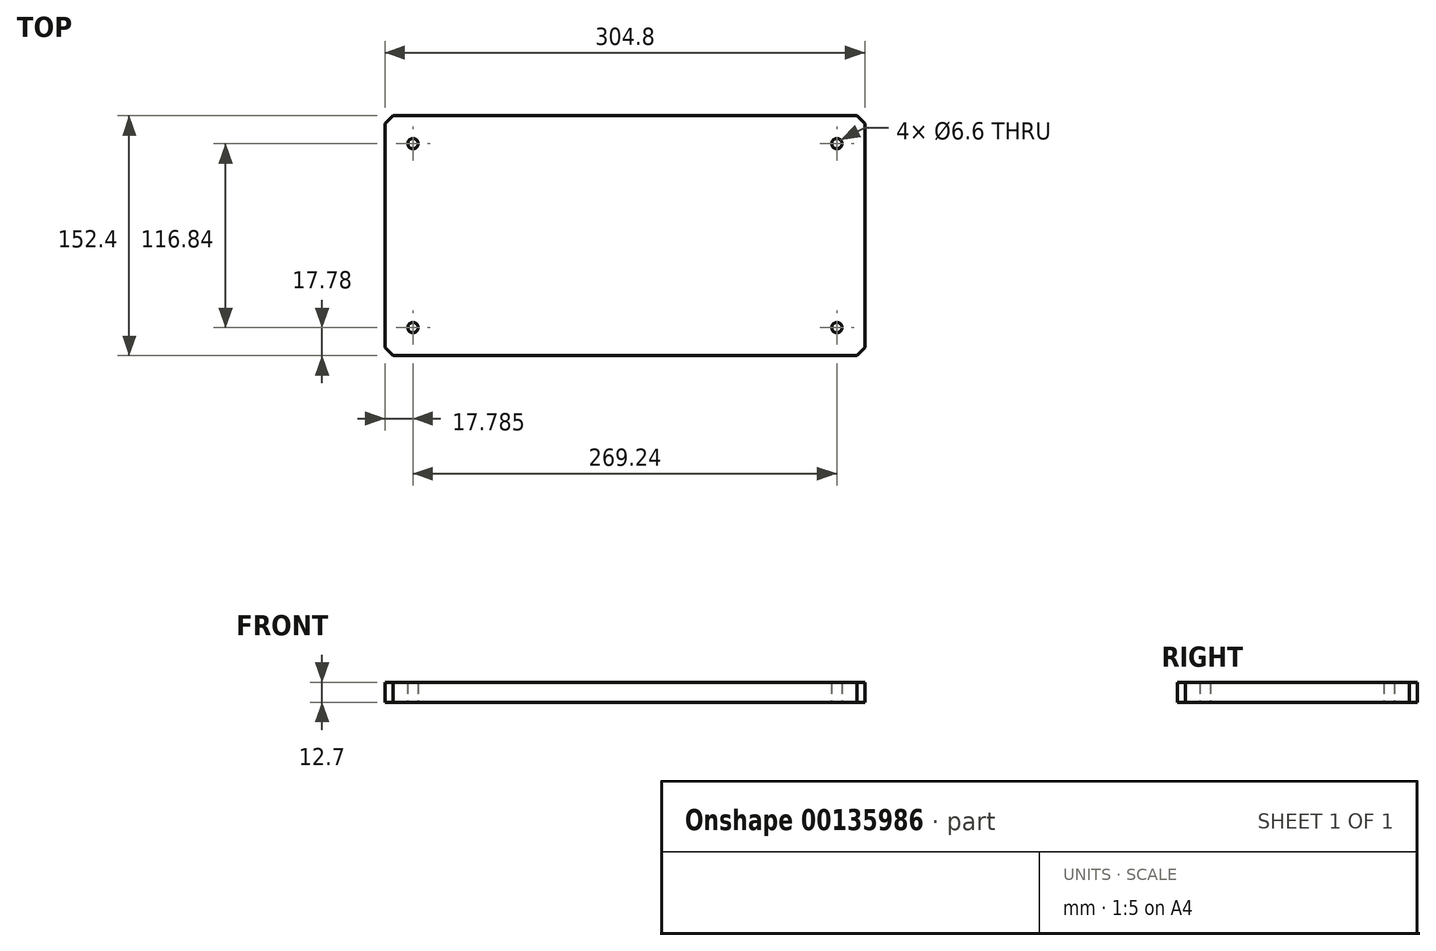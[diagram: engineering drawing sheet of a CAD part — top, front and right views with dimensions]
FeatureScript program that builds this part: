
annotation { "Feature Type Name" : "Feature", "Feature Type Description" : "" }
export const myFeature = defineFeature(function(context is Context, id is Id, definition is map)
    precondition{}
    {
        {
            var Q0;
            Q0=qCreatedBy(makeId("Top.planeOp"),FACE);
            var sketch = newSketch(context, id + "F0", { "sketchPlane" : qUnion([Q0])});
            skLineSegment(sketch, "E0.bottom", {"start": v(-156.77, 77.64) * mm, "end": v(148.03, 77.64) * mm});
            skLineSegment(sketch, "E0.top", {"start": v(-156.77, -74.76) * mm, "end": v(148.03, -74.76) * mm});
            skLineSegment(sketch, "E0.left", {"start": v(-156.77, 77.64) * mm, "end": v(-156.77, -74.76) * mm});
            skLineSegment(sketch, "E0.right", {"start": v(148.03, 77.64) * mm, "end": v(148.03, -74.76) * mm});
            skPoint(sketch, "E1", {"position": v(-138.99, -56.98) * mm});
            skSolve(sketch);
        }
        {
            var Q0;
            Q0=makeQuery(id+"F0.imprint","IMPRINT",FACE,{"disambiguationData":[TD([[makeQuery(id+"F0.imprint","IMPRINT",EDGE,{"derivedFrom":sQuery(id+"F0.wireOp",EDGE,"E0.bottom")}),-1.0]])]});
            extrude(context, id + "F1", {"entities" : qUnion([Q0]), "depth" : 12.7 * mm});
        }
        {
            var Q0;
            Q0=makeQuery(id+"F1.opExtrude","SWEPT_EDGE",EDGE,{"disambiguationData":[OSD([sQuery(id+"F0.wireOp",EDGE,"E0.top"),sQuery(id+"F0.wireOp",EDGE,"E0.right")])]});
            var Q1;
            Q1=makeQuery(id+"F1.opExtrude","SWEPT_EDGE",EDGE,{"disambiguationData":[OSD([sQuery(id+"F0.wireOp",EDGE,"E0.bottom"),sQuery(id+"F0.wireOp",EDGE,"E0.right")])]});
            var Q2;
            Q2=makeQuery(id+"F1.opExtrude","SWEPT_EDGE",EDGE,{"disambiguationData":[OSD([sQuery(id+"F0.wireOp",EDGE,"E0.bottom"),sQuery(id+"F0.wireOp",EDGE,"E0.left")])]});
            var Q3;
            Q3=makeQuery(id+"F1.opExtrude","SWEPT_EDGE",EDGE,{"disambiguationData":[OSD([sQuery(id+"F0.wireOp",EDGE,"E0.top"),sQuery(id+"F0.wireOp",EDGE,"E0.left")])]});
            chamfer(context, id + "F2", {"entities" : qUnion([Q0, Q1, Q2, Q3]), "width" : 5.08 * mm, "tangentPropagation" : true});
        }
        {
            var Q0;
            Q0=makeQuery(id+"F1.opExtrude","CAP_FACE",FACE,{"disambiguationData":[OSD([sQuery(id+"F0.wireOp",EDGE,"E0.bottom"),sQuery(id+"F0.wireOp",EDGE,"E0.top"),sQuery(id+"F0.wireOp",EDGE,"E0.left"),sQuery(id+"F0.wireOp",EDGE,"E0.right")])],"isStart":true});
            var sketch = newSketch(context, id + "F3", { "sketchPlane" : qUnion([Q0])});
            skPoint(sketch, "E2", {"position": v(-138.99, -59.86) * mm});
            skPoint(sketch, "E3.0.1.0", {"position": v(-138.99, 56.98) * mm});
            skPoint(sketch, "E3.1.0.0", {"position": v(130.25, -59.86) * mm});
            skPoint(sketch, "E3.1.1.0", {"position": v(130.25, 56.98) * mm});
            skLineSegment(sketch, "E3.direction1", {"start": v(-138.99, -59.86) * mm, "end": v(130.25, -59.86) * mm, "construction": true});
            skLineSegment(sketch, "E3.direction2", {"start": v(-138.99, -59.86) * mm, "end": v(-138.99, 56.98) * mm, "construction": true});
            skSolve(sketch);
        }
        {
            var Q0;
            Q0=sQuery(id+"F3.wireOp",VERTEX,"E2");
            var Q1;
            Q1=sQuery(id+"F3.wireOp",VERTEX,"E3.0.1.0");
            var Q2;
            Q2=sQuery(id+"F3.wireOp",VERTEX,"E3.1.1.0");
            var Q3;
            Q3=sQuery(id+"F3.wireOp",VERTEX,"E3.1.0.0");
            var Q4;
            Q4=makeQuery(id+"F1.opExtrude","SWEPT_BODY",BODY,{"disambiguationData":[OSD([sQuery(id+"F0.wireOp",EDGE,"E0.bottom"),sQuery(id+"F0.wireOp",EDGE,"E0.top"),sQuery(id+"F0.wireOp",EDGE,"E0.left"),sQuery(id+"F0.wireOp",EDGE,"E0.right")])]});
            hole(context, id + "F4", {"style" : HoleStyle.SIMPLE, "endStyle" : HoleEndStyle.THROUGH, "standardTappedOrClearance" : lookupTablePath({ "standard" : "ISO", "fit" : "Normal", "size" : "M6", "type" : "Clearance" }), "standardBlindInLast" : lookupTablePath({ "fit" : "Standard", "standard" : "ISO", "size" : "M6", "type" : "Clearance" }), "holeDiameter" : 6.6 * mm, "locations" : qUnion([Q0, Q1, Q2, Q3]), "scope" : qUnion([Q4]), "isTappedThrough" : true});
        }
    });
